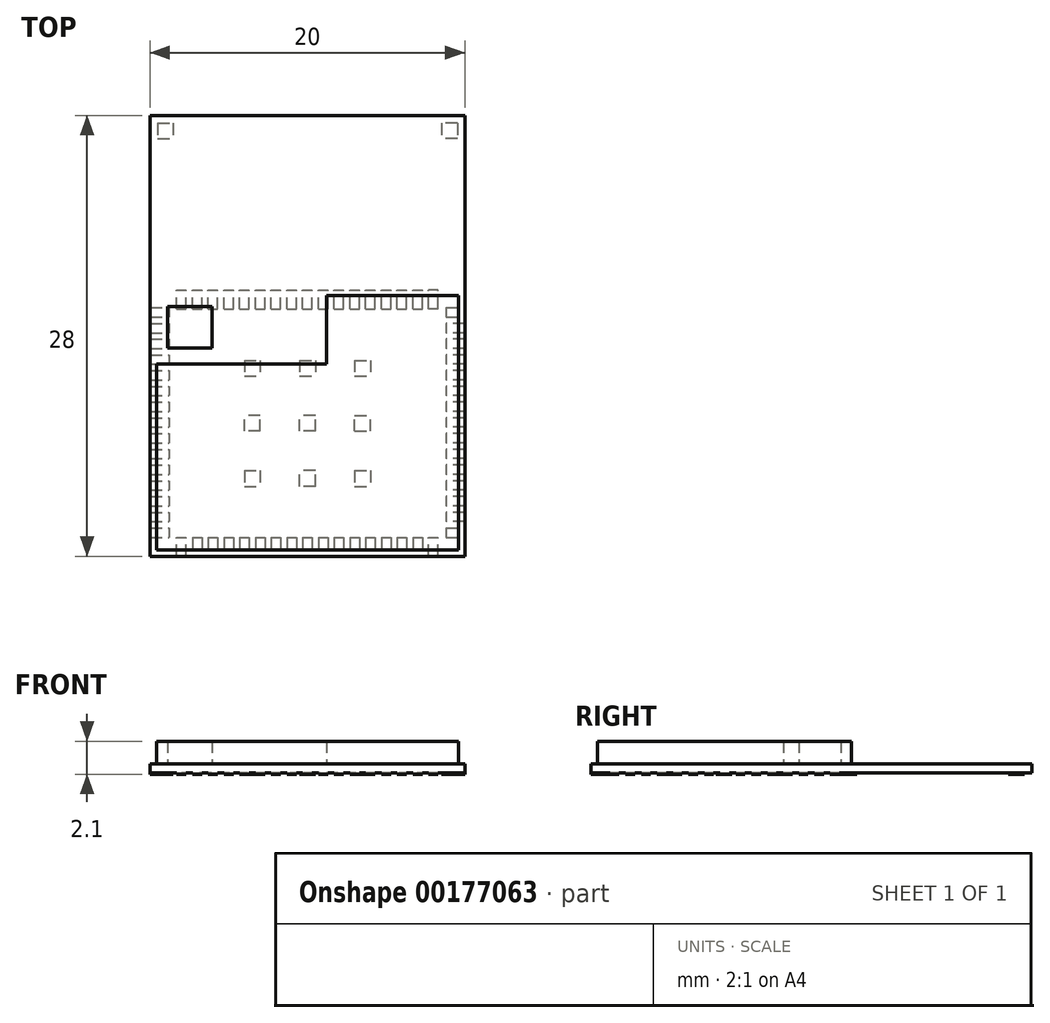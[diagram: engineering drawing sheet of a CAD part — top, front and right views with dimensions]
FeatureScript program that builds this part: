
annotation { "Feature Type Name" : "Feature", "Feature Type Description" : "" }
export const myFeature = defineFeature(function(context is Context, id is Id, definition is map)
    precondition{}
    {
        {
            var Q0;
            Q0=qCreatedBy(makeId("Top.planeOp"),FACE);
            var sketch = newSketch(context, id + "F0", { "sketchPlane" : qUnion([Q0])});
            skLineSegment(sketch, "E0.bottom", {"start": v(10, 14) * mm, "end": v(-10, 14) * mm});
            skLineSegment(sketch, "E0.top", {"start": v(10, -14) * mm, "end": v(-10, -14) * mm});
            skLineSegment(sketch, "E0.left", {"start": v(10, 14) * mm, "end": v(10, -14) * mm});
            skLineSegment(sketch, "E0.right", {"start": v(-10, 14) * mm, "end": v(-10, -14) * mm});
            skPoint(sketch, "E0.middle", {"position": v(0, 0) * mm});
            skSolve(sketch);
        }
        {
            var Q0;
            Q0 = qSketchRegion(id + "F0", true);
            extrude(context, id + "F1", {"entities" : qUnion([Q0]), "depth" : .57 * mm});
        }
        {
            var Q0;
            Q0=makeQuery(id+"F1.opExtrude","CAP_FACE",FACE,{"disambiguationData":[OSD([sQuery(id+"F0.wireOp",EDGE,"E0.bottom"),sQuery(id+"F0.wireOp",EDGE,"E0.top"),sQuery(id+"F0.wireOp",EDGE,"E0.left"),sQuery(id+"F0.wireOp",EDGE,"E0.right")])],"isStart":false});
            var sketch = newSketch(context, id + "F2", { "sketchPlane" : qUnion([Q0])});
            skLineSegment(sketch, "E1", {"start": v(-9.6, -1.78) * mm, "end": v(-9.59, -13.58) * mm});
            skLineSegment(sketch, "E2", {"start": v(-9.59, -13.58) * mm, "end": v(9.6, -13.58) * mm});
            skLineSegment(sketch, "E3", {"start": v(9.6, -13.58) * mm, "end": v(9.6, 2.55) * mm});
            skLineSegment(sketch, "E4", {"start": v(9.59, 2.55) * mm, "end": v(1.2, 2.55) * mm});
            skLineSegment(sketch, "E5", {"start": v(1.2, 2.55) * mm, "end": v(1.2, -1.78) * mm});
            skLineSegment(sketch, "E6", {"start": v(1.2, -1.78) * mm, "end": v(-9.59, -1.78) * mm});
            skPoint(sketch, "E7", {"position": v(0, -13.58) * mm});
            skSolve(sketch);
        }
        {
            var Q0;
            Q0 = qSketchRegion(id + "F2", true);
            extrude(context, id + "F3", {"entities" : qUnion([Q0]), "operationType" : NewBodyOperationType.ADD, "depth" : (2 - .57) * mm});
        }
        {
            var Q0;
            Q0=makeQuery(id+"F1.opExtrude","CAP_FACE",FACE,{"disambiguationData":[OSD([sQuery(id+"F0.wireOp",EDGE,"E0.bottom"),sQuery(id+"F0.wireOp",EDGE,"E0.top"),sQuery(id+"F0.wireOp",EDGE,"E0.left"),sQuery(id+"F0.wireOp",EDGE,"E0.right")])],"isStart":false});
            var sketch = newSketch(context, id + "F4", { "sketchPlane" : qUnion([Q0])});
            skLineSegment(sketch, "E8.bottom", {"start": v(-6.05, -0.78) * mm, "end": v(-8.9, -0.78) * mm});
            skLineSegment(sketch, "E8.top", {"start": v(-6.05, 1.87) * mm, "end": v(-8.9, 1.87) * mm});
            skLineSegment(sketch, "E8.left", {"start": v(-6.05, -0.78) * mm, "end": v(-6.05, 1.87) * mm});
            skLineSegment(sketch, "E8.right", {"start": v(-8.9, -0.78) * mm, "end": v(-8.9, 1.87) * mm});
            skPoint(sketch, "E8.middle", {"position": v(-7.47, 0.54) * mm});
            skSolve(sketch);
        }
        {
            var Q0;
            Q0 = qSketchRegion(id + "F4", true);
            extrude(context, id + "F5", {"entities" : qUnion([Q0]), "operationType" : NewBodyOperationType.ADD, "depth" : (2 - .57) * mm});
        }
        {
            var Q0;
            Q0=qCreatedBy(makeId("Top.planeOp"),FACE);
            var sketch = newSketch(context, id + "F6", { "sketchPlane" : qUnion([Q0])});
            skLineSegment(sketch, "E9.bottom", {"start": v(-9.52, 13.52) * mm, "end": v(-8.52, 13.52) * mm});
            skLineSegment(sketch, "E9.top", {"start": v(-9.52, 12.52) * mm, "end": v(-8.52, 12.52) * mm});
            skLineSegment(sketch, "E9.left", {"start": v(-9.52, 13.52) * mm, "end": v(-9.52, 12.52) * mm});
            skLineSegment(sketch, "E9.right", {"start": v(-8.52, 13.52) * mm, "end": v(-8.52, 12.52) * mm});
            skLineSegment(sketch, "E10.bottom", {"start": v(9.52, 13.52) * mm, "end": v(8.52, 13.52) * mm});
            skLineSegment(sketch, "E10.top", {"start": v(9.52, 12.52) * mm, "end": v(8.52, 12.52) * mm});
            skLineSegment(sketch, "E10.left", {"start": v(9.52, 13.52) * mm, "end": v(9.52, 12.52) * mm});
            skLineSegment(sketch, "E10.right", {"start": v(8.52, 13.52) * mm, "end": v(8.52, 12.52) * mm});
            skLineSegment(sketch, "E11.bottom", {"start": v(-10, 1.8) * mm, "end": v(-8.8, 1.8) * mm});
            skLineSegment(sketch, "E11.top", {"start": v(-10, 1.2) * mm, "end": v(-8.8, 1.2) * mm});
            skLineSegment(sketch, "E11.left", {"start": v(-10, 1.8) * mm, "end": v(-10, 1.2) * mm});
            skLineSegment(sketch, "E11.right", {"start": v(-8.8, 1.8) * mm, "end": v(-8.8, 1.2) * mm});
            skLineSegment(sketch, "E12.bottom", {"start": v(-10, -12.2) * mm, "end": v(-8.8, -12.2) * mm});
            skLineSegment(sketch, "E12.top", {"start": v(-10, -12.8) * mm, "end": v(-8.8, -12.8) * mm});
            skLineSegment(sketch, "E12.left", {"start": v(-10, -12.2) * mm, "end": v(-10, -12.8) * mm});
            skLineSegment(sketch, "E12.right", {"start": v(-8.8, -12.2) * mm, "end": v(-8.8, -12.8) * mm});
            skLineSegment(sketch, "E13.bottom", {"start": v(-8.3, -14) * mm, "end": v(-7.7, -14) * mm});
            skLineSegment(sketch, "E13.top", {"start": v(-8.3, -12.8) * mm, "end": v(-7.7, -12.8) * mm});
            skLineSegment(sketch, "E13.left", {"start": v(-8.3, -14) * mm, "end": v(-8.3, -12.8) * mm});
            skLineSegment(sketch, "E13.right", {"start": v(-7.7, -14) * mm, "end": v(-7.7, -12.8) * mm});
            skLineSegment(sketch, "E14.bottom", {"start": v(7.7, -14) * mm, "end": v(8.3, -14) * mm});
            skLineSegment(sketch, "E14.top", {"start": v(7.7, -12.8) * mm, "end": v(8.3, -12.8) * mm});
            skLineSegment(sketch, "E14.left", {"start": v(7.7, -14) * mm, "end": v(7.7, -12.8) * mm});
            skLineSegment(sketch, "E14.right", {"start": v(8.3, -14) * mm, "end": v(8.3, -12.8) * mm});
            skLineSegment(sketch, "E15.bottom", {"start": v(8.8, -12.2) * mm, "end": v(10, -12.2) * mm});
            skLineSegment(sketch, "E15.top", {"start": v(8.8, -12.8) * mm, "end": v(10, -12.8) * mm});
            skLineSegment(sketch, "E15.left", {"start": v(8.8, -12.2) * mm, "end": v(8.8, -12.8) * mm});
            skLineSegment(sketch, "E15.right", {"start": v(10, -12.2) * mm, "end": v(10, -12.8) * mm});
            skLineSegment(sketch, "E16.bottom", {"start": v(8.8, 1.8) * mm, "end": v(10, 1.8) * mm});
            skLineSegment(sketch, "E16.top", {"start": v(8.8, 1.2) * mm, "end": v(10, 1.2) * mm});
            skLineSegment(sketch, "E16.left", {"start": v(8.8, 1.8) * mm, "end": v(8.8, 1.2) * mm});
            skLineSegment(sketch, "E16.right", {"start": v(10, 1.8) * mm, "end": v(10, 1.2) * mm});
            skLineSegment(sketch, "E17.bottom", {"start": v(8.3, 1.7) * mm, "end": v(7.7, 1.7) * mm});
            skLineSegment(sketch, "E17.top", {"start": v(8.3, 2.9) * mm, "end": v(7.7, 2.9) * mm});
            skLineSegment(sketch, "E17.left", {"start": v(8.3, 1.7) * mm, "end": v(8.3, 2.9) * mm});
            skLineSegment(sketch, "E17.right", {"start": v(7.7, 1.7) * mm, "end": v(7.7, 2.9) * mm});
            skLineSegment(sketch, "E18.bottom", {"start": v(-8.3, 1.7) * mm, "end": v(-7.7, 1.7) * mm});
            skLineSegment(sketch, "E18.top", {"start": v(-8.3, 2.9) * mm, "end": v(-7.7, 2.9) * mm});
            skLineSegment(sketch, "E18.left", {"start": v(-8.3, 1.7) * mm, "end": v(-8.3, 2.9) * mm});
            skLineSegment(sketch, "E18.right", {"start": v(-7.7, 1.7) * mm, "end": v(-7.7, 2.9) * mm});
            skLineSegment(sketch, "E19.bottom", {"start": v(-4, -1.55) * mm, "end": v(-3, -1.55) * mm});
            skLineSegment(sketch, "E19.top", {"start": v(-4, -2.55) * mm, "end": v(-3, -2.55) * mm});
            skLineSegment(sketch, "E19.left", {"start": v(-4, -1.55) * mm, "end": v(-4, -2.55) * mm});
            skLineSegment(sketch, "E19.right", {"start": v(-3, -1.55) * mm, "end": v(-3, -2.55) * mm});
            skLineSegment(sketch, "E20.bottom", {"start": v(-4, -8.55) * mm, "end": v(-3, -8.55) * mm});
            skLineSegment(sketch, "E20.top", {"start": v(-4, -9.55) * mm, "end": v(-3, -9.55) * mm});
            skLineSegment(sketch, "E20.left", {"start": v(-4, -8.55) * mm, "end": v(-4, -9.55) * mm});
            skLineSegment(sketch, "E20.right", {"start": v(-3, -8.55) * mm, "end": v(-3, -9.55) * mm});
            skLineSegment(sketch, "E21.bottom", {"start": v(3, -1.55) * mm, "end": v(4, -1.55) * mm});
            skLineSegment(sketch, "E21.top", {"start": v(3, -2.55) * mm, "end": v(4, -2.55) * mm});
            skLineSegment(sketch, "E21.left", {"start": v(3, -1.55) * mm, "end": v(3, -2.55) * mm});
            skLineSegment(sketch, "E21.right", {"start": v(4, -1.55) * mm, "end": v(4, -2.55) * mm});
            skLineSegment(sketch, "E22.bottom", {"start": v(3, -8.55) * mm, "end": v(4, -8.55) * mm});
            skLineSegment(sketch, "E22.top", {"start": v(3, -9.55) * mm, "end": v(4, -9.55) * mm});
            skLineSegment(sketch, "E22.left", {"start": v(3, -8.55) * mm, "end": v(3, -9.55) * mm});
            skLineSegment(sketch, "E22.right", {"start": v(4, -8.55) * mm, "end": v(4, -9.55) * mm});
            skLineSegment(sketch, "E23", {"start": v(0, -14) * mm, "end": v(0, 13.92) * mm, "construction": true});
            skLineSegment(sketch, "E24.bottom", {"start": v(-3, -2.55) * mm, "end": v(3, -2.55) * mm, "construction": true});
            skLineSegment(sketch, "E24.top", {"start": v(-3, -8.55) * mm, "end": v(3, -8.55) * mm, "construction": true});
            skLineSegment(sketch, "E24.left", {"start": v(-3, -2.55) * mm, "end": v(-3, -8.55) * mm, "construction": true});
            skLineSegment(sketch, "E24.right", {"start": v(3, -2.55) * mm, "end": v(3, -8.55) * mm, "construction": true});
            skPoint(sketch, "E24.middle", {"position": v(0, -5.55) * mm});
            skLineSegment(sketch, "E25.bottom", {"start": v(-0.5, -1.55) * mm, "end": v(0.5, -1.55) * mm});
            skLineSegment(sketch, "E25.top", {"start": v(-0.5, -2.55) * mm, "end": v(0.5, -2.55) * mm});
            skLineSegment(sketch, "E25.left", {"start": v(-0.5, -1.55) * mm, "end": v(-0.5, -2.55) * mm});
            skLineSegment(sketch, "E25.right", {"start": v(0.5, -1.55) * mm, "end": v(0.5, -2.55) * mm});
            skPoint(sketch, "E25.middle", {"position": v(0, -2.05) * mm});
            skLineSegment(sketch, "E26", {"start": v(10.33, -5.55) * mm, "end": v(-10, -5.55) * mm, "construction": true});
            skLineSegment(sketch, "E27.bottom", {"start": v(-3, -6.05) * mm, "end": v(-4, -6.05) * mm});
            skLineSegment(sketch, "E27.top", {"start": v(-3, -5.05) * mm, "end": v(-4, -5.05) * mm});
            skLineSegment(sketch, "E27.left", {"start": v(-3, -6.05) * mm, "end": v(-3, -5.05) * mm});
            skLineSegment(sketch, "E27.right", {"start": v(-4, -6.05) * mm, "end": v(-4, -5.05) * mm});
            skPoint(sketch, "E27.middle", {"position": v(-3.5, -5.55) * mm});
            skLineSegment(sketch, "E28.bottom", {"start": v(3, -6.05) * mm, "end": v(4, -6.05) * mm});
            skLineSegment(sketch, "E28.top", {"start": v(3, -5.05) * mm, "end": v(4, -5.05) * mm});
            skLineSegment(sketch, "E28.left", {"start": v(3, -6.05) * mm, "end": v(3, -5.05) * mm});
            skLineSegment(sketch, "E28.right", {"start": v(4, -6.05) * mm, "end": v(4, -5.05) * mm});
            skPoint(sketch, "E28.middle", {"position": v(3.5, -5.55) * mm});
            skLineSegment(sketch, "E29.bottom", {"start": v(0.5, -9.55) * mm, "end": v(-0.5, -9.55) * mm});
            skLineSegment(sketch, "E29.top", {"start": v(0.5, -8.55) * mm, "end": v(-0.5, -8.55) * mm});
            skLineSegment(sketch, "E29.left", {"start": v(0.5, -9.55) * mm, "end": v(0.5, -8.55) * mm});
            skLineSegment(sketch, "E29.right", {"start": v(-0.5, -9.55) * mm, "end": v(-0.5, -8.55) * mm});
            skPoint(sketch, "E29.middle", {"position": v(0, -9.05) * mm});
            skLineSegment(sketch, "E30.bottom", {"start": v(0.5, -6.05) * mm, "end": v(-0.5, -6.05) * mm});
            skLineSegment(sketch, "E30.top", {"start": v(0.5, -5.05) * mm, "end": v(-0.5, -5.05) * mm});
            skLineSegment(sketch, "E30.left", {"start": v(0.5, -6.05) * mm, "end": v(0.5, -5.05) * mm});
            skLineSegment(sketch, "E30.right", {"start": v(-0.5, -6.05) * mm, "end": v(-0.5, -5.05) * mm});
            skLineSegment(sketch, "E31.1.0.0", {"start": v(-7.3, 2.9) * mm, "end": v(-6.7, 2.9) * mm});
            skLineSegment(sketch, "E31.1.0.1", {"start": v(-7.3, 1.7) * mm, "end": v(-6.7, 1.7) * mm});
            skLineSegment(sketch, "E31.1.0.2", {"start": v(-7.3, 1.7) * mm, "end": v(-7.3, 2.9) * mm});
            skLineSegment(sketch, "E31.1.0.3", {"start": v(-6.7, 1.7) * mm, "end": v(-6.7, 2.9) * mm});
            skLineSegment(sketch, "E31.2.0.0", {"start": v(-6.3, 2.9) * mm, "end": v(-5.7, 2.9) * mm});
            skLineSegment(sketch, "E31.2.0.1", {"start": v(-6.3, 1.7) * mm, "end": v(-5.7, 1.7) * mm});
            skLineSegment(sketch, "E31.2.0.2", {"start": v(-6.3, 1.7) * mm, "end": v(-6.3, 2.9) * mm});
            skLineSegment(sketch, "E31.2.0.3", {"start": v(-5.7, 1.7) * mm, "end": v(-5.7, 2.9) * mm});
            skLineSegment(sketch, "E31.3.0.0", {"start": v(-5.3, 2.9) * mm, "end": v(-4.7, 2.9) * mm});
            skLineSegment(sketch, "E31.3.0.1", {"start": v(-5.3, 1.7) * mm, "end": v(-4.7, 1.7) * mm});
            skLineSegment(sketch, "E31.3.0.2", {"start": v(-5.3, 1.7) * mm, "end": v(-5.3, 2.9) * mm});
            skLineSegment(sketch, "E31.3.0.3", {"start": v(-4.7, 1.7) * mm, "end": v(-4.7, 2.9) * mm});
            skLineSegment(sketch, "E31.4.0.0", {"start": v(-4.3, 2.9) * mm, "end": v(-3.7, 2.9) * mm});
            skLineSegment(sketch, "E31.4.0.1", {"start": v(-4.3, 1.7) * mm, "end": v(-3.7, 1.7) * mm});
            skLineSegment(sketch, "E31.4.0.2", {"start": v(-4.3, 1.7) * mm, "end": v(-4.3, 2.9) * mm});
            skLineSegment(sketch, "E31.4.0.3", {"start": v(-3.7, 1.7) * mm, "end": v(-3.7, 2.9) * mm});
            skLineSegment(sketch, "E31.5.0.0", {"start": v(-3.3, 2.9) * mm, "end": v(-2.7, 2.9) * mm});
            skLineSegment(sketch, "E31.5.0.1", {"start": v(-3.3, 1.7) * mm, "end": v(-2.7, 1.7) * mm});
            skLineSegment(sketch, "E31.5.0.2", {"start": v(-3.3, 1.7) * mm, "end": v(-3.3, 2.9) * mm});
            skLineSegment(sketch, "E31.5.0.3", {"start": v(-2.7, 1.7) * mm, "end": v(-2.7, 2.9) * mm});
            skLineSegment(sketch, "E31.6.0.0", {"start": v(-2.3, 2.9) * mm, "end": v(-1.7, 2.9) * mm});
            skLineSegment(sketch, "E31.6.0.1", {"start": v(-2.3, 1.7) * mm, "end": v(-1.7, 1.7) * mm});
            skLineSegment(sketch, "E31.6.0.2", {"start": v(-2.3, 1.7) * mm, "end": v(-2.3, 2.9) * mm});
            skLineSegment(sketch, "E31.6.0.3", {"start": v(-1.7, 1.7) * mm, "end": v(-1.7, 2.9) * mm});
            skLineSegment(sketch, "E31.7.0.0", {"start": v(-1.3, 2.9) * mm, "end": v(-0.7, 2.9) * mm});
            skLineSegment(sketch, "E31.7.0.1", {"start": v(-1.3, 1.7) * mm, "end": v(-0.7, 1.7) * mm});
            skLineSegment(sketch, "E31.7.0.2", {"start": v(-1.3, 1.7) * mm, "end": v(-1.3, 2.9) * mm});
            skLineSegment(sketch, "E31.7.0.3", {"start": v(-0.7, 1.7) * mm, "end": v(-0.7, 2.9) * mm});
            skLineSegment(sketch, "E31.8.0.0", {"start": v(-0.3, 2.9) * mm, "end": v(0.3, 2.9) * mm});
            skLineSegment(sketch, "E31.8.0.1", {"start": v(-0.3, 1.7) * mm, "end": v(0.3, 1.7) * mm});
            skLineSegment(sketch, "E31.8.0.2", {"start": v(-0.3, 1.7) * mm, "end": v(-0.3, 2.9) * mm});
            skLineSegment(sketch, "E31.8.0.3", {"start": v(0.3, 1.7) * mm, "end": v(0.3, 2.9) * mm});
            skLineSegment(sketch, "E31.9.0.0", {"start": v(0.7, 2.9) * mm, "end": v(1.3, 2.9) * mm});
            skLineSegment(sketch, "E31.9.0.1", {"start": v(0.7, 1.7) * mm, "end": v(1.3, 1.7) * mm});
            skLineSegment(sketch, "E31.9.0.2", {"start": v(0.7, 1.7) * mm, "end": v(0.7, 2.9) * mm});
            skLineSegment(sketch, "E31.9.0.3", {"start": v(1.3, 1.7) * mm, "end": v(1.3, 2.9) * mm});
            skLineSegment(sketch, "E31.10.0.0", {"start": v(1.7, 2.9) * mm, "end": v(2.3, 2.9) * mm});
            skLineSegment(sketch, "E31.10.0.1", {"start": v(1.7, 1.7) * mm, "end": v(2.3, 1.7) * mm});
            skLineSegment(sketch, "E31.10.0.2", {"start": v(1.7, 1.7) * mm, "end": v(1.7, 2.9) * mm});
            skLineSegment(sketch, "E31.10.0.3", {"start": v(2.3, 1.7) * mm, "end": v(2.3, 2.9) * mm});
            skLineSegment(sketch, "E31.11.0.0", {"start": v(2.7, 2.9) * mm, "end": v(3.3, 2.9) * mm});
            skLineSegment(sketch, "E31.11.0.1", {"start": v(2.7, 1.7) * mm, "end": v(3.3, 1.7) * mm});
            skLineSegment(sketch, "E31.11.0.2", {"start": v(2.7, 1.7) * mm, "end": v(2.7, 2.9) * mm});
            skLineSegment(sketch, "E31.11.0.3", {"start": v(3.3, 1.7) * mm, "end": v(3.3, 2.9) * mm});
            skLineSegment(sketch, "E31.12.0.0", {"start": v(3.7, 2.9) * mm, "end": v(4.3, 2.9) * mm});
            skLineSegment(sketch, "E31.12.0.1", {"start": v(3.7, 1.7) * mm, "end": v(4.3, 1.7) * mm});
            skLineSegment(sketch, "E31.12.0.2", {"start": v(3.7, 1.7) * mm, "end": v(3.7, 2.9) * mm});
            skLineSegment(sketch, "E31.12.0.3", {"start": v(4.3, 1.7) * mm, "end": v(4.3, 2.9) * mm});
            skLineSegment(sketch, "E31.13.0.0", {"start": v(4.7, 2.9) * mm, "end": v(5.3, 2.9) * mm});
            skLineSegment(sketch, "E31.13.0.1", {"start": v(4.7, 1.7) * mm, "end": v(5.3, 1.7) * mm});
            skLineSegment(sketch, "E31.13.0.2", {"start": v(4.7, 1.7) * mm, "end": v(4.7, 2.9) * mm});
            skLineSegment(sketch, "E31.13.0.3", {"start": v(5.3, 1.7) * mm, "end": v(5.3, 2.9) * mm});
            skLineSegment(sketch, "E31.14.0.0", {"start": v(5.7, 2.9) * mm, "end": v(6.3, 2.9) * mm});
            skLineSegment(sketch, "E31.14.0.1", {"start": v(5.7, 1.7) * mm, "end": v(6.3, 1.7) * mm});
            skLineSegment(sketch, "E31.14.0.2", {"start": v(5.7, 1.7) * mm, "end": v(5.7, 2.9) * mm});
            skLineSegment(sketch, "E31.14.0.3", {"start": v(6.3, 1.7) * mm, "end": v(6.3, 2.9) * mm});
            skLineSegment(sketch, "E31.15.0.0", {"start": v(6.7, 2.9) * mm, "end": v(7.3, 2.9) * mm});
            skLineSegment(sketch, "E31.15.0.1", {"start": v(6.7, 1.7) * mm, "end": v(7.3, 1.7) * mm});
            skLineSegment(sketch, "E31.15.0.2", {"start": v(6.7, 1.7) * mm, "end": v(6.7, 2.9) * mm});
            skLineSegment(sketch, "E31.15.0.3", {"start": v(7.3, 1.7) * mm, "end": v(7.3, 2.9) * mm});
            skLineSegment(sketch, "E31.direction1", {"start": v(-8.3, 1.7) * mm, "end": v(-7.3, 1.7) * mm, "construction": true});
            skLineSegment(sketch, "E32.1.0.0", {"start": v(-8.8, 0.8) * mm, "end": v(-8.8, 0.2) * mm});
            skLineSegment(sketch, "E32.1.0.1", {"start": v(-10, 0.8) * mm, "end": v(-10, 0.2) * mm});
            skLineSegment(sketch, "E32.1.0.2", {"start": v(-10, 0.2) * mm, "end": v(-8.8, 0.2) * mm});
            skLineSegment(sketch, "E32.1.0.3", {"start": v(-10, 0.8) * mm, "end": v(-8.8, 0.8) * mm});
            skLineSegment(sketch, "E32.2.0.0", {"start": v(-8.8, -0.2) * mm, "end": v(-8.8, -0.8) * mm});
            skLineSegment(sketch, "E32.2.0.1", {"start": v(-10, -0.2) * mm, "end": v(-10, -0.8) * mm});
            skLineSegment(sketch, "E32.2.0.2", {"start": v(-10, -0.8) * mm, "end": v(-8.8, -0.8) * mm});
            skLineSegment(sketch, "E32.2.0.3", {"start": v(-10, -0.2) * mm, "end": v(-8.8, -0.2) * mm});
            skLineSegment(sketch, "E32.3.0.0", {"start": v(-8.8, -1.2) * mm, "end": v(-8.8, -1.8) * mm});
            skLineSegment(sketch, "E32.3.0.1", {"start": v(-10, -1.2) * mm, "end": v(-10, -1.8) * mm});
            skLineSegment(sketch, "E32.3.0.2", {"start": v(-10, -1.8) * mm, "end": v(-8.8, -1.8) * mm});
            skLineSegment(sketch, "E32.3.0.3", {"start": v(-10, -1.2) * mm, "end": v(-8.8, -1.2) * mm});
            skLineSegment(sketch, "E32.4.0.0", {"start": v(-8.8, -2.2) * mm, "end": v(-8.8, -2.8) * mm});
            skLineSegment(sketch, "E32.4.0.1", {"start": v(-10, -2.2) * mm, "end": v(-10, -2.8) * mm});
            skLineSegment(sketch, "E32.4.0.2", {"start": v(-10, -2.8) * mm, "end": v(-8.8, -2.8) * mm});
            skLineSegment(sketch, "E32.4.0.3", {"start": v(-10, -2.2) * mm, "end": v(-8.8, -2.2) * mm});
            skLineSegment(sketch, "E32.5.0.0", {"start": v(-8.8, -3.2) * mm, "end": v(-8.8, -3.8) * mm});
            skLineSegment(sketch, "E32.5.0.1", {"start": v(-10, -3.2) * mm, "end": v(-10, -3.8) * mm});
            skLineSegment(sketch, "E32.5.0.2", {"start": v(-10, -3.8) * mm, "end": v(-8.8, -3.8) * mm});
            skLineSegment(sketch, "E32.5.0.3", {"start": v(-10, -3.2) * mm, "end": v(-8.8, -3.2) * mm});
            skLineSegment(sketch, "E32.6.0.0", {"start": v(-8.8, -4.2) * mm, "end": v(-8.8, -4.8) * mm});
            skLineSegment(sketch, "E32.6.0.1", {"start": v(-10, -4.2) * mm, "end": v(-10, -4.8) * mm});
            skLineSegment(sketch, "E32.6.0.2", {"start": v(-10, -4.8) * mm, "end": v(-8.8, -4.8) * mm});
            skLineSegment(sketch, "E32.6.0.3", {"start": v(-10, -4.2) * mm, "end": v(-8.8, -4.2) * mm});
            skLineSegment(sketch, "E32.7.0.0", {"start": v(-8.8, -5.2) * mm, "end": v(-8.8, -5.8) * mm});
            skLineSegment(sketch, "E32.7.0.1", {"start": v(-10, -5.2) * mm, "end": v(-10, -5.8) * mm});
            skLineSegment(sketch, "E32.7.0.2", {"start": v(-10, -5.8) * mm, "end": v(-8.8, -5.8) * mm});
            skLineSegment(sketch, "E32.7.0.3", {"start": v(-10, -5.2) * mm, "end": v(-8.8, -5.2) * mm});
            skLineSegment(sketch, "E32.8.0.0", {"start": v(-8.8, -6.2) * mm, "end": v(-8.8, -6.8) * mm});
            skLineSegment(sketch, "E32.8.0.1", {"start": v(-10, -6.2) * mm, "end": v(-10, -6.8) * mm});
            skLineSegment(sketch, "E32.8.0.2", {"start": v(-10, -6.8) * mm, "end": v(-8.8, -6.8) * mm});
            skLineSegment(sketch, "E32.8.0.3", {"start": v(-10, -6.2) * mm, "end": v(-8.8, -6.2) * mm});
            skLineSegment(sketch, "E32.9.0.0", {"start": v(-8.8, -7.2) * mm, "end": v(-8.8, -7.8) * mm});
            skLineSegment(sketch, "E32.9.0.1", {"start": v(-10, -7.2) * mm, "end": v(-10, -7.8) * mm});
            skLineSegment(sketch, "E32.9.0.2", {"start": v(-10, -7.8) * mm, "end": v(-8.8, -7.8) * mm});
            skLineSegment(sketch, "E32.9.0.3", {"start": v(-10, -7.2) * mm, "end": v(-8.8, -7.2) * mm});
            skLineSegment(sketch, "E32.10.0.0", {"start": v(-8.8, -8.2) * mm, "end": v(-8.8, -8.8) * mm});
            skLineSegment(sketch, "E32.10.0.1", {"start": v(-10, -8.2) * mm, "end": v(-10, -8.8) * mm});
            skLineSegment(sketch, "E32.10.0.2", {"start": v(-10, -8.8) * mm, "end": v(-8.8, -8.8) * mm});
            skLineSegment(sketch, "E32.10.0.3", {"start": v(-10, -8.2) * mm, "end": v(-8.8, -8.2) * mm});
            skLineSegment(sketch, "E32.11.0.0", {"start": v(-8.8, -9.2) * mm, "end": v(-8.8, -9.8) * mm});
            skLineSegment(sketch, "E32.11.0.1", {"start": v(-10, -9.2) * mm, "end": v(-10, -9.8) * mm});
            skLineSegment(sketch, "E32.11.0.2", {"start": v(-10, -9.8) * mm, "end": v(-8.8, -9.8) * mm});
            skLineSegment(sketch, "E32.11.0.3", {"start": v(-10, -9.2) * mm, "end": v(-8.8, -9.2) * mm});
            skLineSegment(sketch, "E32.12.0.0", {"start": v(-8.8, -10.2) * mm, "end": v(-8.8, -10.8) * mm});
            skLineSegment(sketch, "E32.12.0.1", {"start": v(-10, -10.2) * mm, "end": v(-10, -10.8) * mm});
            skLineSegment(sketch, "E32.12.0.2", {"start": v(-10, -10.8) * mm, "end": v(-8.8, -10.8) * mm});
            skLineSegment(sketch, "E32.12.0.3", {"start": v(-10, -10.2) * mm, "end": v(-8.8, -10.2) * mm});
            skLineSegment(sketch, "E32.13.0.0", {"start": v(-8.8, -11.2) * mm, "end": v(-8.8, -11.8) * mm});
            skLineSegment(sketch, "E32.13.0.1", {"start": v(-10, -11.2) * mm, "end": v(-10, -11.8) * mm});
            skLineSegment(sketch, "E32.13.0.2", {"start": v(-10, -11.8) * mm, "end": v(-8.8, -11.8) * mm});
            skLineSegment(sketch, "E32.13.0.3", {"start": v(-10, -11.2) * mm, "end": v(-8.8, -11.2) * mm});
            skLineSegment(sketch, "E32.direction1", {"start": v(-10, 1.2) * mm, "end": v(-10, 0.2) * mm, "construction": true});
            skLineSegment(sketch, "E33.MirrorCS", {"start": v(1.7, -12.8) * mm, "end": v(2.3, -12.8) * mm});
            skLineSegment(sketch, "E34.MirrorCS", {"start": v(-2.3, -12.8) * mm, "end": v(-1.7, -12.8) * mm});
            skLineSegment(sketch, "E35.MirrorCS", {"start": v(-6.3, -12.8) * mm, "end": v(-5.7, -12.8) * mm});
            skLineSegment(sketch, "E36.MirrorCS", {"start": v(5.7, -12.8) * mm, "end": v(6.3, -12.8) * mm});
            skLineSegment(sketch, "E37.MirrorCS", {"start": v(2.7, -14) * mm, "end": v(3.3, -14) * mm});
            skLineSegment(sketch, "E38.MirrorCS", {"start": v(-1.3, -14) * mm, "end": v(-0.7, -14) * mm});
            skLineSegment(sketch, "E39.MirrorCS", {"start": v(-5.3, -14) * mm, "end": v(-4.7, -14) * mm});
            skLineSegment(sketch, "E40.MirrorCS", {"start": v(6.7, -14) * mm, "end": v(7.3, -14) * mm});
            skLineSegment(sketch, "E41.MirrorCS", {"start": v(1.7, -14) * mm, "end": v(2.3, -14) * mm});
            skLineSegment(sketch, "E42.MirrorCS", {"start": v(-2.3, -14) * mm, "end": v(-1.7, -14) * mm});
            skLineSegment(sketch, "E43.MirrorCS", {"start": v(5.7, -14) * mm, "end": v(6.3, -14) * mm});
            skLineSegment(sketch, "E44.MirrorCS", {"start": v(-6.3, -14) * mm, "end": v(-5.7, -14) * mm});
            skLineSegment(sketch, "E45.MirrorCS", {"start": v(-3.3, -12.8) * mm, "end": v(-2.7, -12.8) * mm});
            skLineSegment(sketch, "E46.MirrorCS", {"start": v(0.7, -12.8) * mm, "end": v(1.3, -12.8) * mm});
            skLineSegment(sketch, "E47.MirrorCS", {"start": v(4.7, -12.8) * mm, "end": v(5.3, -12.8) * mm});
            skLineSegment(sketch, "E48.MirrorCS", {"start": v(-3.3, -14) * mm, "end": v(-2.7, -14) * mm});
            skLineSegment(sketch, "E49.MirrorCS", {"start": v(0.7, -14) * mm, "end": v(1.3, -14) * mm});
            skLineSegment(sketch, "E50.MirrorCS", {"start": v(4.7, -14) * mm, "end": v(5.3, -14) * mm});
            skLineSegment(sketch, "E51.MirrorCS", {"start": v(2.7, -12.8) * mm, "end": v(3.3, -12.8) * mm});
            skLineSegment(sketch, "E52.MirrorCS", {"start": v(-1.3, -12.8) * mm, "end": v(-0.7, -12.8) * mm});
            skLineSegment(sketch, "E53.MirrorCS", {"start": v(3.7, -14) * mm, "end": v(4.3, -14) * mm});
            skLineSegment(sketch, "E54.MirrorCS", {"start": v(-5.3, -12.8) * mm, "end": v(-4.7, -12.8) * mm});
            skLineSegment(sketch, "E55.MirrorCS", {"start": v(-0.3, -14) * mm, "end": v(0.3, -14) * mm});
            skLineSegment(sketch, "E56.MirrorCS", {"start": v(-4.3, -14) * mm, "end": v(-3.7, -14) * mm});
            skLineSegment(sketch, "E57.MirrorCS", {"start": v(6.7, -12.8) * mm, "end": v(7.3, -12.8) * mm});
            skLineSegment(sketch, "E58.MirrorCS", {"start": v(-4.3, -12.8) * mm, "end": v(-3.7, -12.8) * mm});
            skLineSegment(sketch, "E59.MirrorCS", {"start": v(-0.3, -12.8) * mm, "end": v(0.3, -12.8) * mm});
            skLineSegment(sketch, "E60.MirrorCS", {"start": v(3.7, -12.8) * mm, "end": v(4.3, -12.8) * mm});
            skLineSegment(sketch, "E61.MirrorCS", {"start": v(1.7, -12.8) * mm, "end": v(1.7, -14) * mm});
            skLineSegment(sketch, "E62.MirrorCS", {"start": v(-2.3, -12.8) * mm, "end": v(-2.3, -14) * mm});
            skLineSegment(sketch, "E63.MirrorCS", {"start": v(-6.3, -12.8) * mm, "end": v(-6.3, -14) * mm});
            skLineSegment(sketch, "E64.MirrorCS", {"start": v(5.7, -12.8) * mm, "end": v(5.7, -14) * mm});
            skLineSegment(sketch, "E65.MirrorCS", {"start": v(2.3, -12.8) * mm, "end": v(2.3, -14) * mm});
            skLineSegment(sketch, "E66.MirrorCS", {"start": v(-1.7, -12.8) * mm, "end": v(-1.7, -14) * mm});
            skLineSegment(sketch, "E67.MirrorCS", {"start": v(-5.7, -12.8) * mm, "end": v(-5.7, -14) * mm});
            skLineSegment(sketch, "E68.MirrorCS", {"start": v(6.3, -12.8) * mm, "end": v(6.3, -14) * mm});
            skLineSegment(sketch, "E69.MirrorCS", {"start": v(-2.7, -12.8) * mm, "end": v(-2.7, -14) * mm});
            skLineSegment(sketch, "E70.MirrorCS", {"start": v(1.3, -12.8) * mm, "end": v(1.3, -14) * mm});
            skLineSegment(sketch, "E71.MirrorCS", {"start": v(5.3, -12.8) * mm, "end": v(5.3, -14) * mm});
            skLineSegment(sketch, "E72.MirrorCS", {"start": v(-6.7, -12.8) * mm, "end": v(-6.7, -14) * mm});
            skLineSegment(sketch, "E73.MirrorCS", {"start": v(-3.3, -12.8) * mm, "end": v(-3.3, -14) * mm});
            skLineSegment(sketch, "E74.MirrorCS", {"start": v(0.7, -12.8) * mm, "end": v(0.7, -14) * mm});
            skLineSegment(sketch, "E75.MirrorCS", {"start": v(4.7, -12.8) * mm, "end": v(4.7, -14) * mm});
            skLineSegment(sketch, "E76.MirrorCS", {"start": v(-7.3, -12.8) * mm, "end": v(-7.3, -14) * mm});
            skLineSegment(sketch, "E77.MirrorCS", {"start": v(-7.3, -12.8) * mm, "end": v(-6.7, -12.8) * mm});
            skLineSegment(sketch, "E78.MirrorCS", {"start": v(-7.3, -14) * mm, "end": v(-6.7, -14) * mm});
            skLineSegment(sketch, "E79.MirrorCS", {"start": v(6.7, -12.8) * mm, "end": v(6.7, -14) * mm});
            skLineSegment(sketch, "E80.MirrorCS", {"start": v(4.3, -12.8) * mm, "end": v(4.3, -14) * mm});
            skLineSegment(sketch, "E81.MirrorCS", {"start": v(3.7, -12.8) * mm, "end": v(3.7, -14) * mm});
            skLineSegment(sketch, "E82.MirrorCS", {"start": v(-0.3, -12.8) * mm, "end": v(-0.3, -14) * mm});
            skLineSegment(sketch, "E83.MirrorCS", {"start": v(-4.3, -12.8) * mm, "end": v(-4.3, -14) * mm});
            skLineSegment(sketch, "E84.MirrorCS", {"start": v(-3.7, -12.8) * mm, "end": v(-3.7, -14) * mm});
            skLineSegment(sketch, "E85.MirrorCS", {"start": v(0.3, -12.8) * mm, "end": v(0.3, -14) * mm});
            skLineSegment(sketch, "E86.MirrorCS", {"start": v(-5.3, -12.8) * mm, "end": v(-5.3, -14) * mm});
            skLineSegment(sketch, "E87.MirrorCS", {"start": v(-1.3, -12.8) * mm, "end": v(-1.3, -14) * mm});
            skLineSegment(sketch, "E88.MirrorCS", {"start": v(2.7, -12.8) * mm, "end": v(2.7, -14) * mm});
            skLineSegment(sketch, "E89.MirrorCS", {"start": v(7.3, -12.8) * mm, "end": v(7.3, -14) * mm});
            skLineSegment(sketch, "E90.MirrorCS", {"start": v(3.3, -12.8) * mm, "end": v(3.3, -14) * mm});
            skLineSegment(sketch, "E91.MirrorCS", {"start": v(-0.7, -12.8) * mm, "end": v(-0.7, -14) * mm});
            skLineSegment(sketch, "E92.MirrorCS", {"start": v(-4.7, -12.8) * mm, "end": v(-4.7, -14) * mm});
            skLineSegment(sketch, "E93.MirrorCS", {"start": v(8.8, 0.8) * mm, "end": v(8.8, 0.2) * mm});
            skLineSegment(sketch, "E94.MirrorCS", {"start": v(8.8, -11.2) * mm, "end": v(8.8, -11.8) * mm});
            skLineSegment(sketch, "E95.MirrorCS", {"start": v(8.8, -7.2) * mm, "end": v(8.8, -7.8) * mm});
            skLineSegment(sketch, "E96.MirrorCS", {"start": v(8.8, -3.2) * mm, "end": v(8.8, -3.8) * mm});
            skLineSegment(sketch, "E97.MirrorCS", {"start": v(10, 0.8) * mm, "end": v(10, 0.2) * mm});
            skLineSegment(sketch, "E98.MirrorCS", {"start": v(10, -11.2) * mm, "end": v(10, -11.8) * mm});
            skLineSegment(sketch, "E99.MirrorCS", {"start": v(10, -7.2) * mm, "end": v(10, -7.8) * mm});
            skLineSegment(sketch, "E100.MirrorCS", {"start": v(10, -3.2) * mm, "end": v(10, -3.8) * mm});
            skLineSegment(sketch, "E101.MirrorCS", {"start": v(8.8, -10.2) * mm, "end": v(8.8, -10.8) * mm});
            skLineSegment(sketch, "E102.MirrorCS", {"start": v(8.8, -6.2) * mm, "end": v(8.8, -6.8) * mm});
            skLineSegment(sketch, "E103.MirrorCS", {"start": v(8.8, -2.2) * mm, "end": v(8.8, -2.8) * mm});
            skLineSegment(sketch, "E104.MirrorCS", {"start": v(10, -1.2) * mm, "end": v(10, -1.8) * mm});
            skLineSegment(sketch, "E105.MirrorCS", {"start": v(10, -5.2) * mm, "end": v(10, -5.8) * mm});
            skLineSegment(sketch, "E106.MirrorCS", {"start": v(10, -9.2) * mm, "end": v(10, -9.8) * mm});
            skLineSegment(sketch, "E107.MirrorCS", {"start": v(8.8, -1.2) * mm, "end": v(8.8, -1.8) * mm});
            skLineSegment(sketch, "E108.MirrorCS", {"start": v(8.8, -5.2) * mm, "end": v(8.8, -5.8) * mm});
            skLineSegment(sketch, "E109.MirrorCS", {"start": v(8.8, -9.2) * mm, "end": v(8.8, -9.8) * mm});
            skLineSegment(sketch, "E110.MirrorCS", {"start": v(10, -0.2) * mm, "end": v(10, -0.8) * mm});
            skLineSegment(sketch, "E111.MirrorCS", {"start": v(8.8, -4.2) * mm, "end": v(8.8, -4.8) * mm});
            skLineSegment(sketch, "E112.MirrorCS", {"start": v(8.8, -8.2) * mm, "end": v(8.8, -8.8) * mm});
            skLineSegment(sketch, "E113.MirrorCS", {"start": v(10, -4.2) * mm, "end": v(10, -4.8) * mm});
            skLineSegment(sketch, "E114.MirrorCS", {"start": v(10, -8.2) * mm, "end": v(10, -8.8) * mm});
            skLineSegment(sketch, "E115.MirrorCS", {"start": v(10, -2.2) * mm, "end": v(10, -2.8) * mm});
            skLineSegment(sketch, "E116.MirrorCS", {"start": v(10, -10.2) * mm, "end": v(10, -10.8) * mm});
            skLineSegment(sketch, "E117.MirrorCS", {"start": v(8.8, -0.2) * mm, "end": v(8.8, -0.8) * mm});
            skLineSegment(sketch, "E118.MirrorCS", {"start": v(10, -6.2) * mm, "end": v(10, -6.8) * mm});
            skLineSegment(sketch, "E119.MirrorCS", {"start": v(10, -10.8) * mm, "end": v(8.8, -10.8) * mm});
            skLineSegment(sketch, "E120.MirrorCS", {"start": v(10, -6.8) * mm, "end": v(8.8, -6.8) * mm});
            skLineSegment(sketch, "E121.MirrorCS", {"start": v(10, -2.8) * mm, "end": v(8.8, -2.8) * mm});
            skLineSegment(sketch, "E122.MirrorCS", {"start": v(10, -10.2) * mm, "end": v(8.8, -10.2) * mm});
            skLineSegment(sketch, "E123.MirrorCS", {"start": v(10, -6.2) * mm, "end": v(8.8, -6.2) * mm});
            skLineSegment(sketch, "E124.MirrorCS", {"start": v(10, -2.2) * mm, "end": v(8.8, -2.2) * mm});
            skLineSegment(sketch, "E125.MirrorCS", {"start": v(10, -9.8) * mm, "end": v(8.8, -9.8) * mm});
            skLineSegment(sketch, "E126.MirrorCS", {"start": v(10, -5.8) * mm, "end": v(8.8, -5.8) * mm});
            skLineSegment(sketch, "E127.MirrorCS", {"start": v(10, -1.8) * mm, "end": v(8.8, -1.8) * mm});
            skLineSegment(sketch, "E128.MirrorCS", {"start": v(10, -9.2) * mm, "end": v(8.8, -9.2) * mm});
            skLineSegment(sketch, "E129.MirrorCS", {"start": v(10, -5.2) * mm, "end": v(8.8, -5.2) * mm});
            skLineSegment(sketch, "E130.MirrorCS", {"start": v(10, -1.2) * mm, "end": v(8.8, -1.2) * mm});
            skLineSegment(sketch, "E131.MirrorCS", {"start": v(10, 0.2) * mm, "end": v(8.8, 0.2) * mm});
            skLineSegment(sketch, "E132.MirrorCS", {"start": v(10, -4.2) * mm, "end": v(8.8, -4.2) * mm});
            skLineSegment(sketch, "E133.MirrorCS", {"start": v(10, -8.2) * mm, "end": v(8.8, -8.2) * mm});
            skLineSegment(sketch, "E134.MirrorCS", {"start": v(10, -0.2) * mm, "end": v(8.8, -0.2) * mm});
            skLineSegment(sketch, "E135.MirrorCS", {"start": v(10, -4.8) * mm, "end": v(8.8, -4.8) * mm});
            skLineSegment(sketch, "E136.MirrorCS", {"start": v(10, -8.8) * mm, "end": v(8.8, -8.8) * mm});
            skLineSegment(sketch, "E137.MirrorCS", {"start": v(10, -0.8) * mm, "end": v(8.8, -0.8) * mm});
            skLineSegment(sketch, "E138.MirrorCS", {"start": v(10, -11.8) * mm, "end": v(8.8, -11.8) * mm});
            skLineSegment(sketch, "E139.MirrorCS", {"start": v(10, -7.8) * mm, "end": v(8.8, -7.8) * mm});
            skLineSegment(sketch, "E140.MirrorCS", {"start": v(10, -3.8) * mm, "end": v(8.8, -3.8) * mm});
            skLineSegment(sketch, "E141.MirrorCS", {"start": v(10, -3.2) * mm, "end": v(8.8, -3.2) * mm});
            skLineSegment(sketch, "E142.MirrorCS", {"start": v(10, -7.2) * mm, "end": v(8.8, -7.2) * mm});
            skLineSegment(sketch, "E143.MirrorCS", {"start": v(10, 0.8) * mm, "end": v(8.8, 0.8) * mm});
            skLineSegment(sketch, "E144.MirrorCS", {"start": v(10, -11.2) * mm, "end": v(8.8, -11.2) * mm});
            skSolve(sketch);
        }
        {
            var Q0;
            Q0 = qSketchRegion(id + "F6", true);
            extrude(context, id + "F7", {"entities" : qUnion([Q0]), "operationType" : NewBodyOperationType.ADD, "oppositeDirection" : true, "depth" : .1 * mm});
        }
    });
